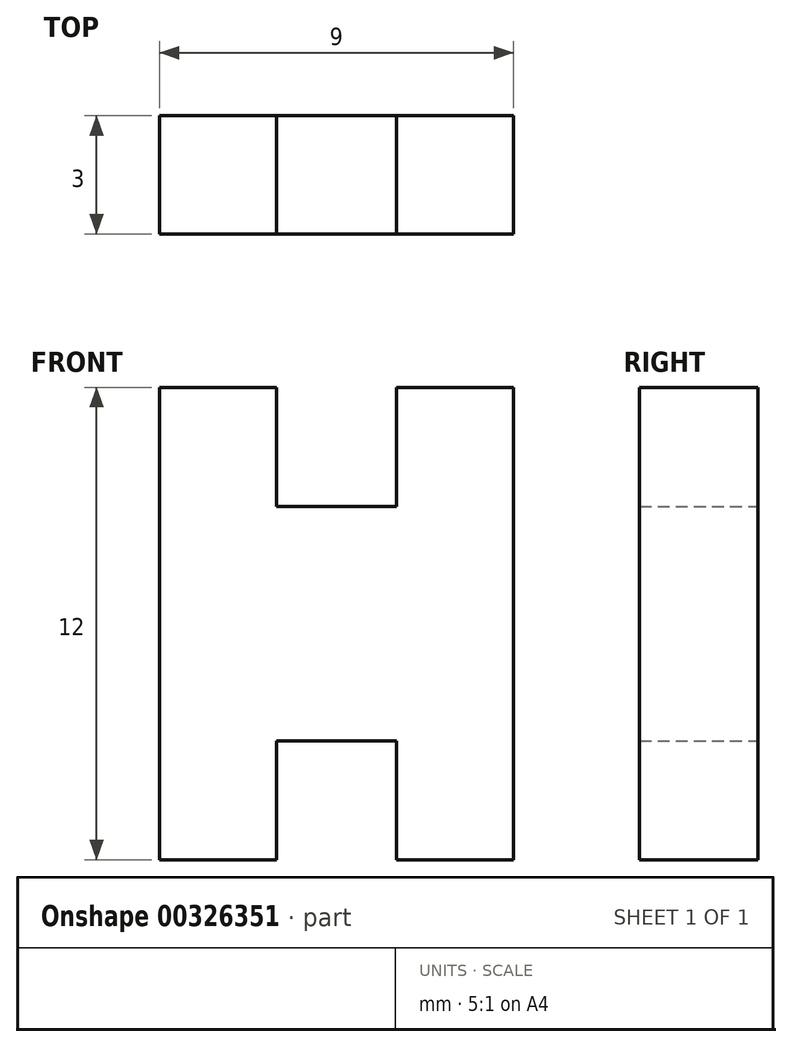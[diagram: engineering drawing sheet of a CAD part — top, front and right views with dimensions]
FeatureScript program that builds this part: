
annotation { "Feature Type Name" : "Feature", "Feature Type Description" : "" }
export const myFeature = defineFeature(function(context is Context, id is Id, definition is map)
    precondition{}
    {
        {
            var Q0;
            Q0=qCreatedBy(makeId("Front.planeOp"),FACE);
            var sketch = newSketch(context, id + "F0", { "sketchPlane" : qUnion([Q0])});
            skLineSegment(sketch, "E0", {"start": v(4.5, 12) * mm, "end": v(4.5, 0) * mm});
            skLineSegment(sketch, "E1", {"start": v(4.5, 0) * mm, "end": v(1.52, 0) * mm});
            skLineSegment(sketch, "E2", {"start": v(1.52, 0) * mm, "end": v(1.52, 3.02) * mm});
            skLineSegment(sketch, "E3", {"start": v(1.52, 3.02) * mm, "end": v(-1.52, 3.02) * mm});
            skLineSegment(sketch, "E4", {"start": v(-1.52, 3.02) * mm, "end": v(-1.52, 0) * mm});
            skLineSegment(sketch, "E5", {"start": v(-1.52, 0) * mm, "end": v(-4.5, 0) * mm});
            skLineSegment(sketch, "E6", {"start": v(-4.5, 0) * mm, "end": v(-4.5, 12) * mm});
            skLineSegment(sketch, "E7", {"start": v(-4.5, 12) * mm, "end": v(-1.52, 12) * mm});
            skLineSegment(sketch, "E8", {"start": v(-1.52, 12) * mm, "end": v(-1.52, 8.98) * mm});
            skLineSegment(sketch, "E9", {"start": v(-1.52, 8.98) * mm, "end": v(1.52, 8.98) * mm});
            skLineSegment(sketch, "E10", {"start": v(1.52, 8.98) * mm, "end": v(1.52, 12) * mm});
            skLineSegment(sketch, "E11", {"start": v(1.52, 12) * mm, "end": v(4.5, 12) * mm});
            skSolve(sketch);
        }
        {
            var Q0;
            Q0=makeQuery(id+"F0.imprint","IMPRINT",FACE,{"disambiguationData":[TD([[makeQuery(id+"F0.imprint","IMPRINT",EDGE,{"derivedFrom":sQuery(id+"F0.wireOp",EDGE,"E0")}),-1.0]])]});
            extrude(context, id + "F1", {"entities" : qUnion([Q0]), "depth" : 3 * mm});
        }
    });
